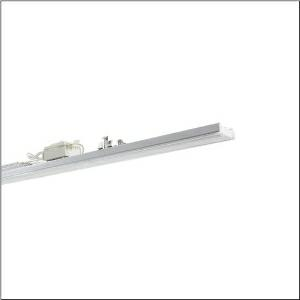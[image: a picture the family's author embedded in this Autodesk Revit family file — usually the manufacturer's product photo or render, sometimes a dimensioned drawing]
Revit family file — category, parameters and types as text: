
# Revit family: licross_21_recessed_mo_52tl14cn485g
name_source: partatom
category: Lighting Fixtures
units: mm (PartAtom-declared; Revit-internal decimal feet)

## family parameters
Cut with Voids When Loaded = No
Host = Face
Light Source = No
Part Type = Normal
Room Calculation Point = No
Round Connector Dimension = Use Diameter
Shared = No

## types (1)
- --- (1 x LED, 8530 lm, 49.9 W, 4000K)
    Apparent Load = 50 VA
    CIE Flux Codes = 56 84 97 100 100
    Color Rendering = 80
    Color Temperature = 4000K
    Default Elevation = 1800 mm
    Description = Licross 21 Recessed MO, luminaire insert, of sheet steel, galvanised, coil coated, white, length: 1.500mm, width: 66mm, height: 67mm, LED rated luminous flux: 8.530lm, light colour: 840, SDCM (Standard Deviation of Colour Matching)MacAdam ≤ 3 SDCM (initial), control gear: ON/OFF Multilumen, CLOi, with plug, 5-pole, with phase selection, mains connection: 220..240V, AC, 50/60Hz, start of lifetime: 50W, end of service life: 61W, internal wiring halogen-free, primary light control with lens, of plastic, primary optical cover: cover, of PMMA, light emission: direct distribution, primary light characteristic: asymmetric, protection rating (complete): IP40, insulation class (complete): insulation class I (protective earthing), certification: CE, ENEC, VDE, UKCA, protection symbol: D if used in an environment without relevant dust loads with corresponding accessories, impact resistance: IK06, permissible ambient temperature for indoor applications: -35..+40°C, corresponds to IFS (International Featured Standards) requirements for safety and quality in the food industry, reducing of maximum allowable ambient temperature of 5°C with ceiling mounting, LABS conformity tested according to VDMA 24364:2018-05, The light source and the operating device comply with the requirements of the Ecodesign Regulation (EU) 2019/2020 and are replaceable in accordance with this regulation, packaging unit: 1 piece
    Height = 58 mm
    Lamp = 1 x LED
    Lamp Light Flux = 8530 lm
    Lamp Power = 49.9 W
    Lamp count = 1
    Length = 1500 mm
    Luminous efficacy = 171 lm/W
    Manufacturer = Siteco
    ModVariant = No
    Model = 52TL14CN485G
    Mounting Place = Ceiling
    Mounting Type = Pendant
    Number of Poles = 1
    OnlyDefault = Yes
    Power Factor = 1
    Product Name = Licross 21 Recessed MO
    Product group = luminaire insert | ceiling pendant
    ProductGroupID = 901
    Protection Class = Protection class I
    Protection Degree = IP 40
    RLX_Detail_Level = 1
    RLX_Emergency_Light_Flux = 0 lm
    RLX_Emergency_Type = 0
    RLX_Emergency_Type_DB = No
    RlxData = <blob elided: 23029 chars, md5=6d667a16>
    Socket = socket
    Standby Power = 0 W
    System Light Flux = 8530 lm
    System Power = 50 W
    Type Comments = factory setting: luminous flux: 100 % | (A | C | E) | 116 mA
    Type Image = l_1296930.jpg
    URL = http://relux.com
    VarID = @adj_110729
    Voltage = 0 V
    Weight = 0.00 kg
    Width = 66 mm

## geometry (parser evidence)
native form markers: Blend x4, Sweep x10
no freeform markers — native parametric forms only
